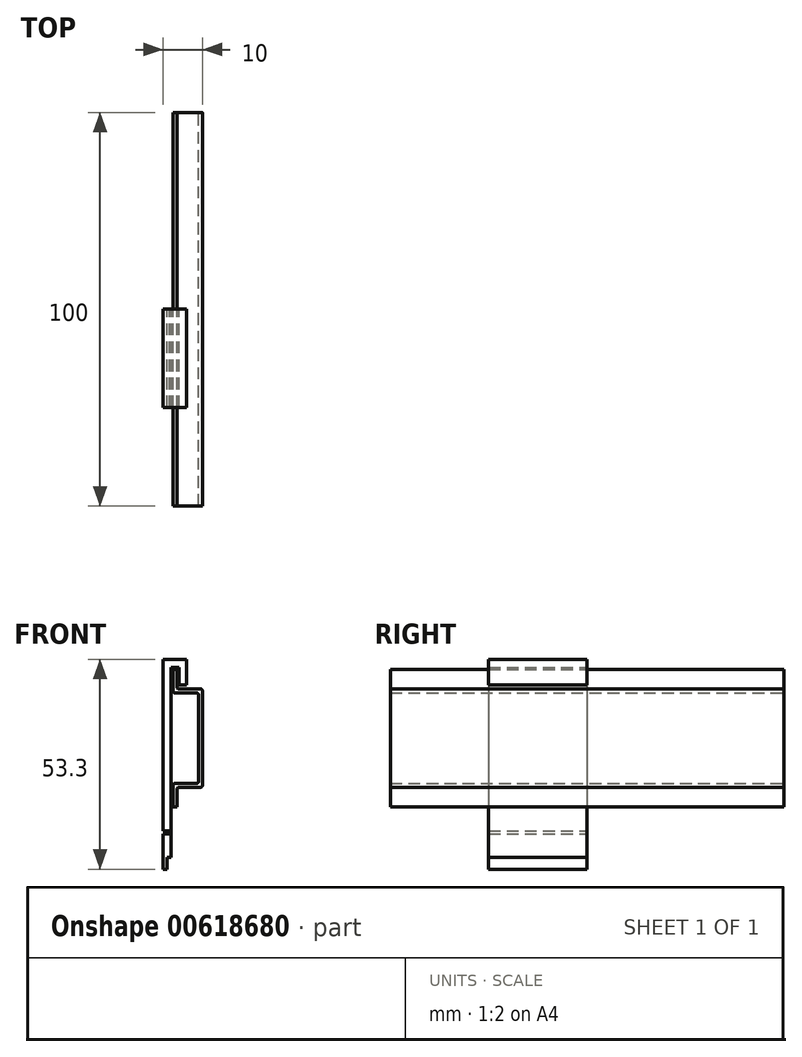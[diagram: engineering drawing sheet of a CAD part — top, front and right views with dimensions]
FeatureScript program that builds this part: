
annotation { "Feature Type Name" : "Feature", "Feature Type Description" : "" }
export const myFeature = defineFeature(function(context is Context, id is Id, definition is map)
    precondition{}
    {
        {
            var Q0;
            Q0=qCreatedBy(makeId("Front.planeOp"),FACE);
            var sketch = newSketch(context, id + "F0", { "sketchPlane" : qUnion([Q0])});
            skLineSegment(sketch, "E0", {"start": v(0, 17.5) * mm, "end": v(0, 13) * mm});
            skLineSegment(sketch, "E1", {"start": v(0.5, 12.5) * mm, "end": v(6, 12.5) * mm});
            skLineSegment(sketch, "E2", {"start": v(6.5, 12) * mm, "end": v(6.5, -12) * mm});
            skLineSegment(sketch, "E3", {"start": v(6, -12.5) * mm, "end": v(0.5, -12.5) * mm});
            skLineSegment(sketch, "E4", {"start": v(0, -13) * mm, "end": v(0, -17.5) * mm});
            skLineSegment(sketch, "E5.0", {"start": v(-1, -12) * mm, "end": v(-1, -17.5) * mm});
            skLineSegment(sketch, "E5.1", {"start": v(-1, 17.5) * mm, "end": v(-1, 12) * mm});
            skLineSegment(sketch, "E5.2", {"start": v(-0.5, 11.5) * mm, "end": v(5, 11.5) * mm});
            skLineSegment(sketch, "E5.3", {"start": v(5.5, 11) * mm, "end": v(5.5, -11) * mm});
            skLineSegment(sketch, "E5.4", {"start": v(5, -11.5) * mm, "end": v(-0.5, -11.5) * mm});
            skLineSegment(sketch, "E6", {"start": v(0, -17.5) * mm, "end": v(-1, -17.5) * mm});
            skLineSegment(sketch, "E7", {"start": v(0, 17.5) * mm, "end": v(-1, 17.5) * mm});
            skPoint(sketch, "E8.visualSharp", {"position": v(-1, 11.5) * mm});
            skArc(sketch, "E8.filletArc", {"start": v(-1, 12) * mm, "mid": v(-0.85, 11.65) * mm, "end": v(-0.5, 11.5) * mm});
            skPoint(sketch, "E9.visualSharp", {"position": v(0, 12.5) * mm});
            skArc(sketch, "E9.filletArc", {"start": v(0, 13) * mm, "mid": v(0.15, 12.65) * mm, "end": v(0.5, 12.5) * mm});
            skPoint(sketch, "E10.visualSharp", {"position": v(-1, -11.5) * mm});
            skArc(sketch, "E10.filletArc", {"start": v(-0.5, -11.5) * mm, "mid": v(-0.85, -11.65) * mm, "end": v(-1, -12) * mm});
            skPoint(sketch, "E11.visualSharp", {"position": v(0, -12.5) * mm});
            skArc(sketch, "E11.filletArc", {"start": v(0.5, -12.5) * mm, "mid": v(0.15, -12.65) * mm, "end": v(0, -13) * mm});
            skPoint(sketch, "E12.visualSharp", {"position": v(5.5, 11.5) * mm});
            skArc(sketch, "E12.filletArc", {"start": v(5.5, 11) * mm, "mid": v(5.35, 11.35) * mm, "end": v(5, 11.5) * mm});
            skPoint(sketch, "E13.visualSharp", {"position": v(6.5, 12.5) * mm});
            skArc(sketch, "E13.filletArc", {"start": v(6.5, 12) * mm, "mid": v(6.35, 12.35) * mm, "end": v(6, 12.5) * mm});
            skPoint(sketch, "E14.visualSharp", {"position": v(5.5, -11.5) * mm});
            skArc(sketch, "E14.filletArc", {"start": v(5, -11.5) * mm, "mid": v(5.35, -11.35) * mm, "end": v(5.5, -11) * mm});
            skPoint(sketch, "E15.visualSharp", {"position": v(6.5, -12.5) * mm});
            skArc(sketch, "E15.filletArc", {"start": v(6, -12.5) * mm, "mid": v(6.35, -12.35) * mm, "end": v(6.5, -12) * mm});
            skSolve(sketch);
        }
        {
            var Q0;
            Q0 = qSketchRegion(id + "F0", true);
            extrude(context, id + "F1", {"entities" : qUnion([Q0]), "depth" : 50 * mm, "offsetDistance" : 25 * mm, "hasSecondDirection" : true, "secondDirectionOppositeDirection" : true, "secondDirectionDepth" : 50 * mm});
        }
        {
            var Q0;
            Q0=qCreatedBy(makeId("Front.planeOp"),FACE);
            var sketch = newSketch(context, id + "F2", { "sketchPlane" : qUnion([Q0])});
            skLineSegment(sketch, "E16", {"start": v(0.5, 15.03) * mm, "end": v(0.5, 18) * mm});
            skLineSegment(sketch, "E17", {"start": v(0.5, 18) * mm, "end": v(-1.5, 18) * mm});
            skLineSegment(sketch, "E18", {"start": v(-1.5, 18) * mm, "end": v(-1.5, -23.5) * mm});
            skLineSegment(sketch, "E19", {"start": v(0.5, 13.5) * mm, "end": v(2.5, 13.5) * mm});
            skLineSegment(sketch, "E20", {"start": v(2.5, 13.5) * mm, "end": v(2.5, 20) * mm});
            skLineSegment(sketch, "E21", {"start": v(2.5, 20) * mm, "end": v(-3.5, 20) * mm});
            skLineSegment(sketch, "E22", {"start": v(-3.5, 20) * mm, "end": v(-3.5, -23.5) * mm});
            skLineSegment(sketch, "E23", {"start": v(0.5, 15.03) * mm, "end": v(0.5, 13.5) * mm});
            skLineSegment(sketch, "E24", {"start": v(-3.5, -23.5) * mm, "end": v(-1.9, -23.5) * mm});
            skLineSegment(sketch, "E25.bottom", {"start": v(-3.5, -24.3) * mm, "end": v(-1.9, -24.3) * mm});
            skLineSegment(sketch, "E25.top", {"start": v(-2.5, -30.3) * mm, "end": v(-1.5, -30.3) * mm});
            skLineSegment(sketch, "E25.left", {"start": v(-3.5, -24.3) * mm, "end": v(-3.5, -30.3) * mm});
            skLineSegment(sketch, "E25.right", {"start": v(-1.5, -24.3) * mm, "end": v(-1.5, -30.3) * mm});
            skLineSegment(sketch, "E26", {"start": v(-1.5, -24.3) * mm, "end": v(-1.5, -23.5) * mm});
            skLineSegment(sketch, "E27", {"start": v(-1.9, -23.5) * mm, "end": v(-1.9, -24.3) * mm});
            skLineSegment(sketch, "E28", {"start": v(-2.5, -30.3) * mm, "end": v(-2.5, -33.3) * mm});
            skLineSegment(sketch, "E29", {"start": v(-2.5, -33.3) * mm, "end": v(-3.5, -33.3) * mm});
            skLineSegment(sketch, "E30", {"start": v(-3.5, -33.3) * mm, "end": v(-3.5, -30.3) * mm});
            skSolve(sketch);
        }
        {
            var Q0;
            Q0 = qSketchRegion(id + "F2", true);
            extrude(context, id + "F3", {"entities" : qUnion([Q0]), "depth" : 25 * mm, "offsetDistance" : 25 * mm});
        }
    });
